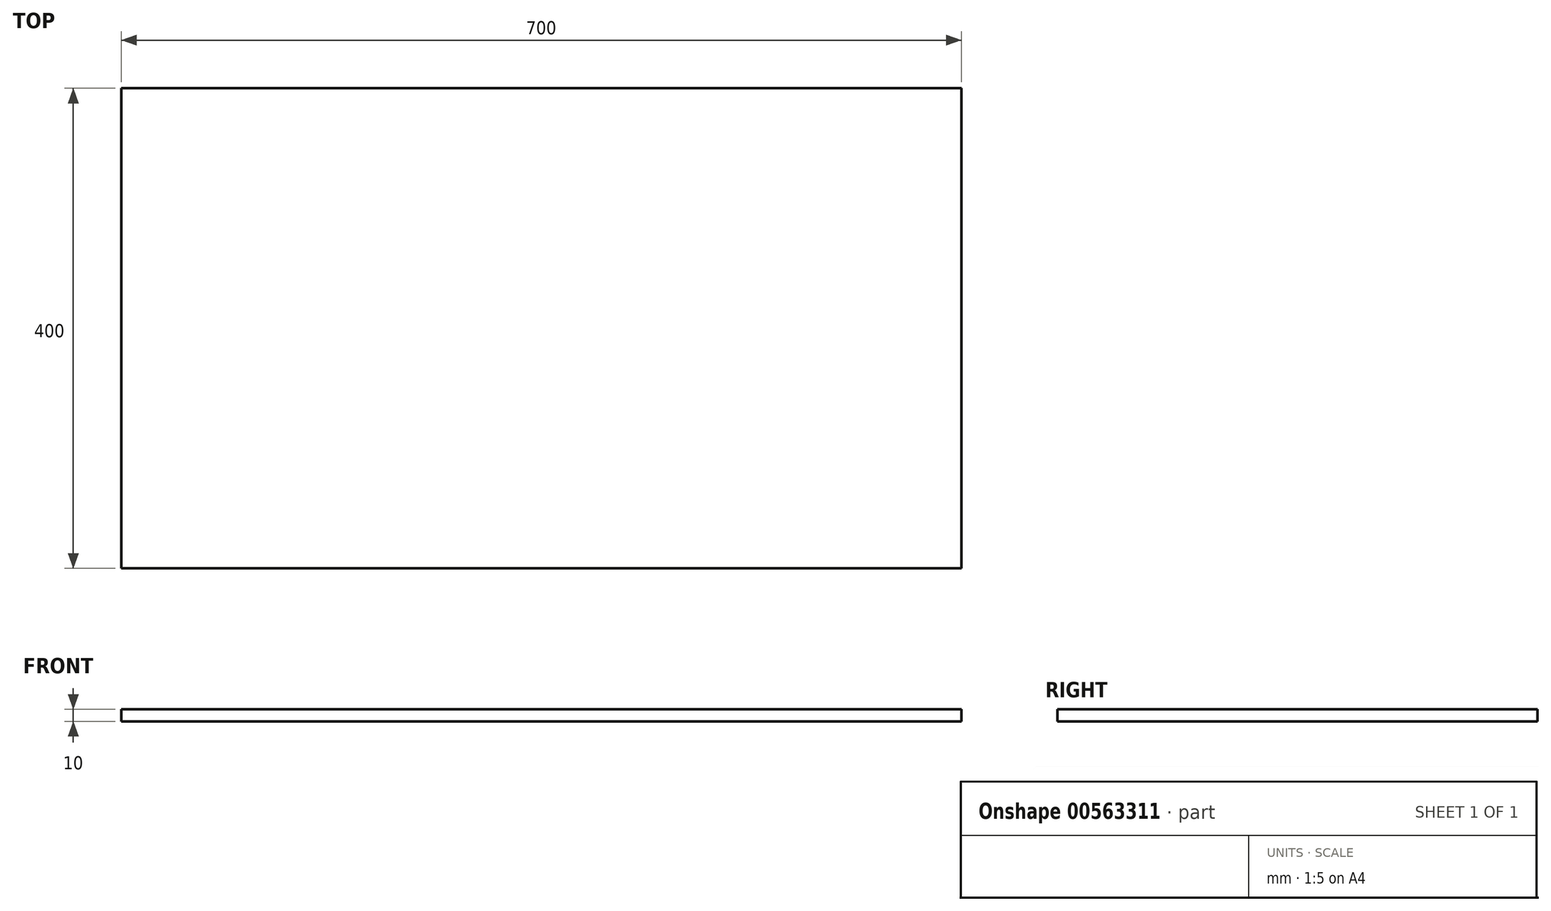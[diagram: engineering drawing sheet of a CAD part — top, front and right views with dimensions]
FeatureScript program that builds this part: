
annotation { "Feature Type Name" : "Feature", "Feature Type Description" : "" }
export const myFeature = defineFeature(function(context is Context, id is Id, definition is map)
    precondition{}
    {
        {
            var Q0;
            Q0=qCreatedBy(makeId("Top.planeOp"),FACE);
            var sketch = newSketch(context, id + "F0", { "sketchPlane" : qUnion([Q0])});
            skLineSegment(sketch, "E0.bottom", {"start": v(-417.52, 186.68) * mm, "end": v(282.48, 186.68) * mm});
            skLineSegment(sketch, "E0.top", {"start": v(-417.52, -213.32) * mm, "end": v(282.48, -213.32) * mm});
            skLineSegment(sketch, "E0.left", {"start": v(-417.52, 186.68) * mm, "end": v(-417.52, -213.32) * mm});
            skLineSegment(sketch, "E0.right", {"start": v(282.48, 186.68) * mm, "end": v(282.48, -213.32) * mm});
            skSolve(sketch);
        }
        {
            var Q0;
            Q0 = qSketchRegion(id + "F0", true);
            extrude(context, id + "F1", {"entities" : qUnion([Q0]), "depth" : 10 * mm, "offsetDistance" : 25 * mm});
        }
    });
